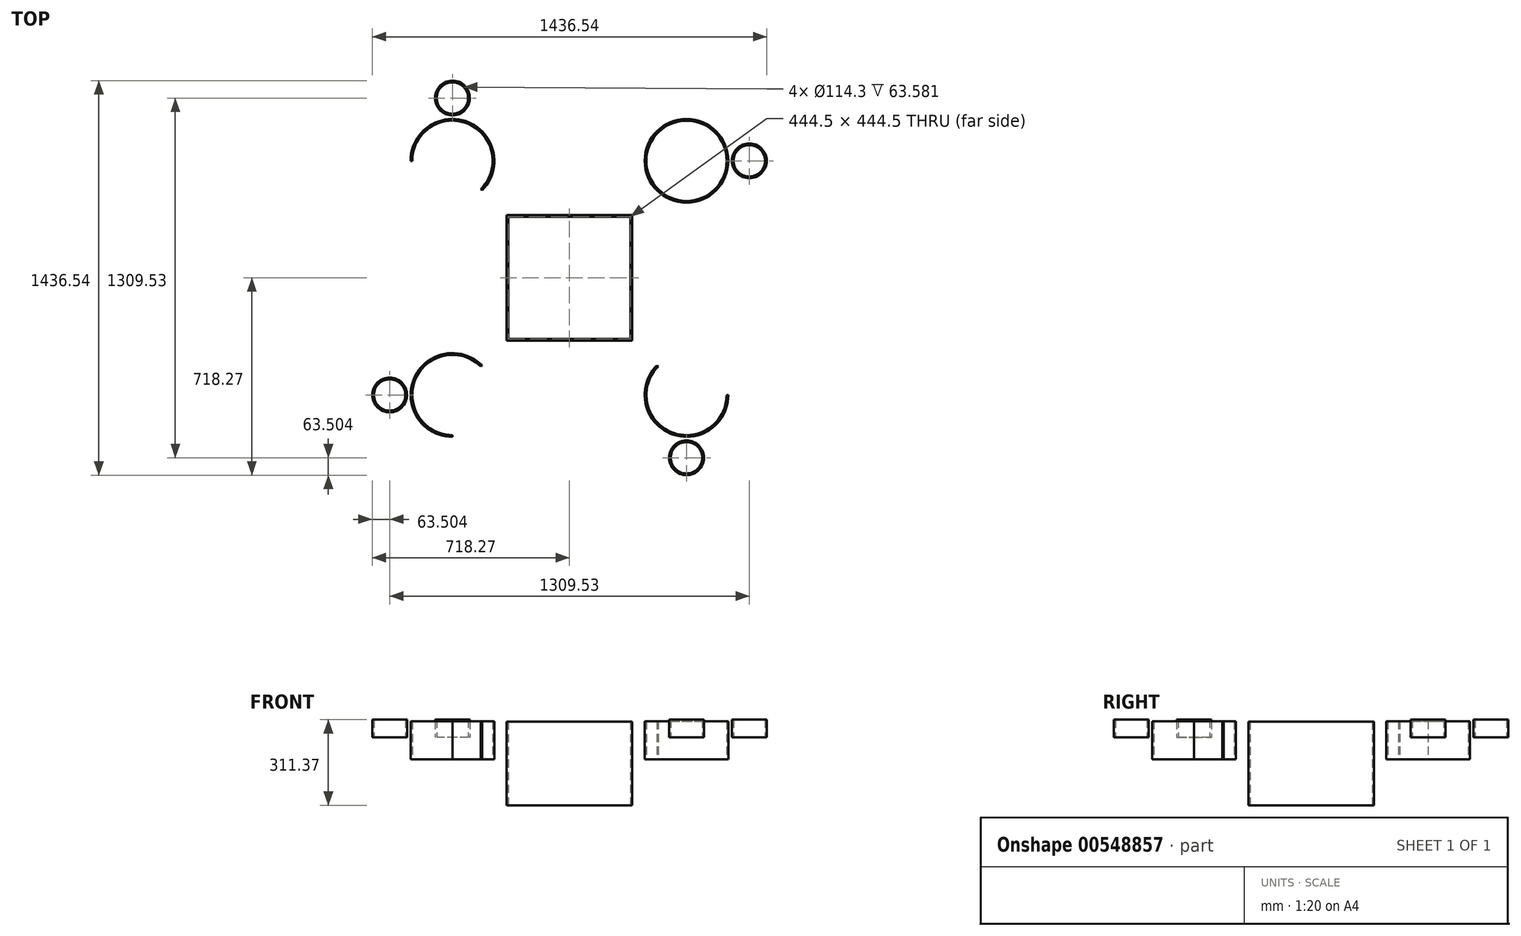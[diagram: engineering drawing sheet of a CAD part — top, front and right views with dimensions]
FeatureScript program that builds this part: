
annotation { "Feature Type Name" : "Feature", "Feature Type Description" : "" }
export const myFeature = defineFeature(function(context is Context, id is Id, definition is map)
    precondition{}
    {
        {
            var Q0;
            Q0=qCreatedBy(makeId("Top.planeOp"),FACE);
            var sketch = newSketch(context, id + "F0", { "sketchPlane" : qUnion([Q0])});
            skLineSegment(sketch, "E0", {"start": v(0, 0) * mm, "end": v(402.27, 0) * mm});
            skLineSegment(sketch, "E1.bottom", {"start": v(228.6, -228.6) * mm, "end": v(-228.6, -228.6) * mm});
            skLineSegment(sketch, "E1.top", {"start": v(228.6, 228.6) * mm, "end": v(-228.6, 228.6) * mm});
            skLineSegment(sketch, "E1.left", {"start": v(228.6, -228.6) * mm, "end": v(228.6, 228.6) * mm});
            skLineSegment(sketch, "E1.right", {"start": v(-228.6, -228.6) * mm, "end": v(-228.6, 228.6) * mm});
            skPoint(sketch, "E1.middle", {"position": v(0, 0) * mm});
            skLineSegment(sketch, "E2", {"start": v(0, 0) * mm, "end": v(228.6, 228.6) * mm});
            skLineSegment(sketch, "E3", {"start": v(228.6, 228.6) * mm, "end": v(426.17, 426.17) * mm});
            skCircle(sketch, "E4", {"center": v(426.17, 426.17) * mm, "radius": 152.4 * mm});
            skLineSegment(sketch, "E5", {"start": v(426.17, 426.17) * mm, "end": v(578.57, 426.17) * mm});
            skLineSegment(sketch, "E6", {"start": v(426.17, 426.17) * mm, "end": v(426.17, 578.57) * mm});
            skLineSegment(sketch, "E7", {"start": v(578.57, 426.17) * mm, "end": v(654.77, 426.17) * mm});
            skCircle(sketch, "E8", {"center": v(654.77, 426.17) * mm, "radius": 63.5 * mm});
            skLineSegment(sketch, "E9.MirrorCS", {"start": v(426.17, 578.57) * mm, "end": v(426.17, 654.77) * mm});
            skCircle(sketch, "E10.MirrorC", {"center": v(426.17, 654.77) * mm, "radius": 63.5 * mm});
            skCircle(sketch, "E11.0", {"center": v(426.17, 426.17) * mm, "radius": 146.05 * mm});
            skCircle(sketch, "E12.0", {"center": v(426.17, 654.77) * mm, "radius": 57.15 * mm});
            skCircle(sketch, "E13.0", {"center": v(654.77, 426.17) * mm, "radius": 57.15 * mm});
            skLineSegment(sketch, "E14.0", {"start": v(222.25, 222.25) * mm, "end": v(-222.25, 222.25) * mm});
            skLineSegment(sketch, "E14.1", {"start": v(222.25, -222.25) * mm, "end": v(222.25, 222.25) * mm});
            skLineSegment(sketch, "E14.2", {"start": v(222.25, -222.25) * mm, "end": v(-222.25, -222.25) * mm});
            skLineSegment(sketch, "E14.3", {"start": v(-222.25, -222.25) * mm, "end": v(-222.25, 222.25) * mm});
            skLineSegment(sketch, "E15.1.0", {"start": v(-426.17, 426.17) * mm, "end": v(-578.57, 426.17) * mm});
            skLineSegment(sketch, "E15.1.1", {"start": v(-426.17, 426.17) * mm, "end": v(-426.17, 578.57) * mm});
            skCircle(sketch, "E15.1.2", {"center": v(-426.17, 654.77) * mm, "radius": 57.15 * mm});
            skLineSegment(sketch, "E15.1.3", {"start": v(-426.17, 426.17) * mm, "end": v(-578.57, 426.17) * mm});
            skCircle(sketch, "E15.1.4", {"center": v(-654.77, 426.17) * mm, "radius": 63.5 * mm});
            skLineSegment(sketch, "E15.1.5", {"start": v(-426.17, 578.57) * mm, "end": v(-426.17, 654.77) * mm});
            skCircle(sketch, "E15.1.6", {"center": v(-426.17, 426.17) * mm, "radius": 146.05 * mm});
            skLineSegment(sketch, "E15.1.7", {"start": v(-228.6, 228.6) * mm, "end": v(-426.17, 426.17) * mm});
            skCircle(sketch, "E15.1.8", {"center": v(-426.17, 654.77) * mm, "radius": 63.5 * mm});
            skLineSegment(sketch, "E15.1.9", {"start": v(-578.57, 426.17) * mm, "end": v(-654.77, 426.17) * mm});
            skCircle(sketch, "E15.1.10", {"center": v(-426.17, 426.17) * mm, "radius": 152.4 * mm});
            skCircle(sketch, "E15.1.11", {"center": v(-654.77, 426.17) * mm, "radius": 57.15 * mm});
            skLineSegment(sketch, "E15.2.0", {"start": v(-426.17, -426.17) * mm, "end": v(-426.17, -578.57) * mm});
            skLineSegment(sketch, "E15.2.1", {"start": v(-426.17, -426.17) * mm, "end": v(-578.57, -426.17) * mm});
            skCircle(sketch, "E15.2.2", {"center": v(-654.77, -426.17) * mm, "radius": 57.15 * mm});
            skLineSegment(sketch, "E15.2.3", {"start": v(-426.17, -426.17) * mm, "end": v(-426.17, -578.57) * mm});
            skCircle(sketch, "E15.2.4", {"center": v(-426.17, -654.77) * mm, "radius": 63.5 * mm});
            skLineSegment(sketch, "E15.2.5", {"start": v(-578.57, -426.17) * mm, "end": v(-654.77, -426.17) * mm});
            skCircle(sketch, "E15.2.6", {"center": v(-426.17, -426.17) * mm, "radius": 146.05 * mm});
            skLineSegment(sketch, "E15.2.7", {"start": v(-228.6, -228.6) * mm, "end": v(-426.17, -426.17) * mm});
            skCircle(sketch, "E15.2.8", {"center": v(-654.77, -426.17) * mm, "radius": 63.5 * mm});
            skLineSegment(sketch, "E15.2.9", {"start": v(-426.17, -578.57) * mm, "end": v(-426.17, -654.77) * mm});
            skCircle(sketch, "E15.2.10", {"center": v(-426.17, -426.17) * mm, "radius": 152.4 * mm});
            skCircle(sketch, "E15.2.11", {"center": v(-426.17, -654.77) * mm, "radius": 57.15 * mm});
            skLineSegment(sketch, "E15.3.0", {"start": v(426.17, -426.17) * mm, "end": v(578.57, -426.17) * mm});
            skLineSegment(sketch, "E15.3.1", {"start": v(426.17, -426.17) * mm, "end": v(426.17, -578.57) * mm});
            skCircle(sketch, "E15.3.2", {"center": v(426.17, -654.77) * mm, "radius": 57.15 * mm});
            skLineSegment(sketch, "E15.3.3", {"start": v(426.17, -426.17) * mm, "end": v(578.57, -426.17) * mm});
            skCircle(sketch, "E15.3.4", {"center": v(654.77, -426.17) * mm, "radius": 63.5 * mm});
            skLineSegment(sketch, "E15.3.5", {"start": v(426.17, -578.57) * mm, "end": v(426.17, -654.77) * mm});
            skCircle(sketch, "E15.3.6", {"center": v(426.17, -426.17) * mm, "radius": 146.05 * mm});
            skLineSegment(sketch, "E15.3.7", {"start": v(228.6, -228.6) * mm, "end": v(426.17, -426.17) * mm});
            skCircle(sketch, "E15.3.8", {"center": v(426.17, -654.77) * mm, "radius": 63.5 * mm});
            skLineSegment(sketch, "E15.3.9", {"start": v(578.57, -426.17) * mm, "end": v(654.77, -426.17) * mm});
            skCircle(sketch, "E15.3.10", {"center": v(426.17, -426.17) * mm, "radius": 152.4 * mm});
            skCircle(sketch, "E15.3.11", {"center": v(654.77, -426.17) * mm, "radius": 57.15 * mm});
            skSolve(sketch);
        }
        {
            var Q0;
            {var subQ1=sQuery(id+"F0.wireOp",EDGE,"E1.bottom");Q0=makeQuery(id+"F0.imprint","IMPRINT",FACE,{"disambiguationData":[TD([[makeQuery(id+"F0.imprint","IMPRINT",EDGE,{"derivedFrom":subQ1}),-1.0]])]});}
            var Q1;
            {var subQ0=sQuery(id+"F0.wireOp",EDGE,"E1.left");var subQ1=sQuery(id+"F0.wireOp",EDGE,"E0");var subQ2=makeQuery(id+"F0.imprint","INTERSECT",VERTEX,{"derivedFrom":[subQ1,subQ0]});Q1=makeQuery(id+"F0.imprint","IMPRINT",FACE,{"disambiguationData":[TD([[makeQuery(id+"F0.imprint","IMPRINT",EDGE,{"disambiguationData":[TD([[subQ2,1.0]])],"derivedFrom":subQ1}),1.0]])]});}
            extrude(context, id + "F1", {"entities" : qUnion([Q0, Q1]), "depth" : 304.8 * mm, "offsetDistance" : 25.4 * mm});
        }
        {
            var Q0;
            {var subQ0=sQuery(id+"F0.wireOp",EDGE,"E15.1.10");var subQ1=sQuery(id+"F0.wireOp",EDGE,"E15.1.1");var subQ2=makeQuery(id+"F0.imprint","INTERSECT",VERTEX,{"derivedFrom":[subQ1,subQ0]});Q0=makeQuery(id+"F0.imprint","IMPRINT",FACE,{"disambiguationData":[TD([[makeQuery(id+"F0.imprint","IMPRINT",EDGE,{"disambiguationData":[TD([[subQ2,1.0]])],"derivedFrom":subQ1}),1.0]])]});}
            var Q1;
            {var subQ0=sQuery(id+"F0.wireOp",EDGE,"E15.1.10");var subQ1=sQuery(id+"F0.wireOp",EDGE,"E15.1.1");var subQ2=makeQuery(id+"F0.imprint","INTERSECT",VERTEX,{"derivedFrom":[subQ1,subQ0]});Q1=makeQuery(id+"F0.imprint","IMPRINT",FACE,{"disambiguationData":[TD([[makeQuery(id+"F0.imprint","IMPRINT",EDGE,{"disambiguationData":[TD([[subQ2,1.0]])],"derivedFrom":subQ1}),-1.0]])]});}
            var Q2;
            {var subQ0=sQuery(id+"F0.wireOp",EDGE,"E15.1.10");var subQ1=sQuery(id+"F0.wireOp",EDGE,"E15.1.3");var subQ2=makeQuery(id+"F0.imprint","INTERSECT",VERTEX,{"derivedFrom":[subQ1,subQ0]});Q2=makeQuery(id+"F0.imprint","IMPRINT",FACE,{"disambiguationData":[TD([[makeQuery(id+"F0.imprint","IMPRINT",EDGE,{"disambiguationData":[TD([[subQ2,1.0]])],"derivedFrom":subQ1}),1.0]])]});}
            var Q3;
            {var subQ0=sQuery(id+"F0.wireOp",EDGE,"E4");var subQ1=sQuery(id+"F0.wireOp",EDGE,"E3");var subQ2=makeQuery(id+"F0.imprint","INTERSECT",VERTEX,{"derivedFrom":[subQ1,subQ0]});Q3=makeQuery(id+"F0.imprint","IMPRINT",FACE,{"disambiguationData":[TD([[makeQuery(id+"F0.imprint","IMPRINT",EDGE,{"disambiguationData":[TD([[subQ2,-1.0]])],"derivedFrom":subQ1}),1.0]])]});}
            var Q4;
            {var subQ0=sQuery(id+"F0.wireOp",EDGE,"E5");var subQ1=sQuery(id+"F0.wireOp",EDGE,"E4");var subQ2=makeQuery(id+"F0.imprint","INTERSECT",VERTEX,{"derivedFrom":[subQ1,subQ0]});Q4=makeQuery(id+"F0.imprint","IMPRINT",FACE,{"disambiguationData":[TD([[makeQuery(id+"F0.imprint","IMPRINT",EDGE,{"disambiguationData":[TD([[subQ2,-1.0]])],"derivedFrom":subQ1}),1.0]])]});}
            var Q5;
            {var subQ0=sQuery(id+"F0.wireOp",EDGE,"E4");var subQ1=sQuery(id+"F0.wireOp",EDGE,"E3");var subQ2=makeQuery(id+"F0.imprint","INTERSECT",VERTEX,{"derivedFrom":[subQ1,subQ0]});Q5=makeQuery(id+"F0.imprint","IMPRINT",FACE,{"disambiguationData":[TD([[makeQuery(id+"F0.imprint","IMPRINT",EDGE,{"disambiguationData":[TD([[subQ2,-1.0]])],"derivedFrom":subQ1}),-1.0]])]});}
            var Q6;
            {var subQ0=sQuery(id+"F0.wireOp",EDGE,"E15.3.10");var subQ1=sQuery(id+"F0.wireOp",EDGE,"E15.3.3");var subQ2=makeQuery(id+"F0.imprint","INTERSECT",VERTEX,{"derivedFrom":[subQ1,subQ0]});Q6=makeQuery(id+"F0.imprint","IMPRINT",FACE,{"disambiguationData":[TD([[makeQuery(id+"F0.imprint","IMPRINT",EDGE,{"disambiguationData":[TD([[subQ2,1.0]])],"derivedFrom":subQ1}),1.0]])]});}
            var Q7;
            {var subQ0=sQuery(id+"F0.wireOp",EDGE,"E15.3.10");var subQ1=sQuery(id+"F0.wireOp",EDGE,"E15.3.1");var subQ2=makeQuery(id+"F0.imprint","INTERSECT",VERTEX,{"derivedFrom":[subQ1,subQ0]});Q7=makeQuery(id+"F0.imprint","IMPRINT",FACE,{"disambiguationData":[TD([[makeQuery(id+"F0.imprint","IMPRINT",EDGE,{"disambiguationData":[TD([[subQ2,1.0]])],"derivedFrom":subQ1}),1.0]])]});}
            var Q8;
            {var subQ0=sQuery(id+"F0.wireOp",EDGE,"E15.3.10");var subQ1=sQuery(id+"F0.wireOp",EDGE,"E15.3.1");var subQ2=makeQuery(id+"F0.imprint","INTERSECT",VERTEX,{"derivedFrom":[subQ1,subQ0]});Q8=makeQuery(id+"F0.imprint","IMPRINT",FACE,{"disambiguationData":[TD([[makeQuery(id+"F0.imprint","IMPRINT",EDGE,{"disambiguationData":[TD([[subQ2,1.0]])],"derivedFrom":subQ1}),-1.0]])]});}
            var Q9;
            {var subQ0=sQuery(id+"F0.wireOp",EDGE,"E15.2.10");var subQ1=sQuery(id+"F0.wireOp",EDGE,"E15.2.1");var subQ2=makeQuery(id+"F0.imprint","INTERSECT",VERTEX,{"derivedFrom":[subQ1,subQ0]});Q9=makeQuery(id+"F0.imprint","IMPRINT",FACE,{"disambiguationData":[TD([[makeQuery(id+"F0.imprint","IMPRINT",EDGE,{"disambiguationData":[TD([[subQ2,1.0]])],"derivedFrom":subQ1}),1.0]])]});}
            var Q10;
            {var subQ0=sQuery(id+"F0.wireOp",EDGE,"E15.2.10");var subQ1=sQuery(id+"F0.wireOp",EDGE,"E15.2.1");var subQ2=makeQuery(id+"F0.imprint","INTERSECT",VERTEX,{"derivedFrom":[subQ1,subQ0]});Q10=makeQuery(id+"F0.imprint","IMPRINT",FACE,{"disambiguationData":[TD([[makeQuery(id+"F0.imprint","IMPRINT",EDGE,{"disambiguationData":[TD([[subQ2,1.0]])],"derivedFrom":subQ1}),-1.0]])]});}
            var Q11;
            {var subQ0=sQuery(id+"F0.wireOp",EDGE,"E15.2.10");var subQ1=sQuery(id+"F0.wireOp",EDGE,"E15.2.3");var subQ2=makeQuery(id+"F0.imprint","INTERSECT",VERTEX,{"derivedFrom":[subQ1,subQ0]});Q11=makeQuery(id+"F0.imprint","IMPRINT",FACE,{"disambiguationData":[TD([[makeQuery(id+"F0.imprint","IMPRINT",EDGE,{"disambiguationData":[TD([[subQ2,1.0]])],"derivedFrom":subQ1}),1.0]])]});}
            extrude(context, id + "F2", {"entities" : qUnion([Q0, Q1, Q2, Q3, Q4, Q5, Q6, Q7, Q8, Q9, Q10, Q11]), "depth" : 305.76 * mm, "offsetDistance" : 25.4 * mm, "hasSecondDirection" : true, "secondDirectionOppositeDirection" : false, "secondDirectionDepth" : 166.62 * mm});
        }
        {
            var Q0;
            Q0=makeQuery(id+"F0.imprint","IMPRINT",FACE,{"disambiguationData":[TD([[makeQuery(id+"F0.imprint","IMPRINT",EDGE,{"derivedFrom":sQuery(id+"F0.wireOp",EDGE,"E15.1.2")}),-1.0]])]});
            var Q1;
            Q1=makeQuery(id+"F0.imprint","IMPRINT",FACE,{"disambiguationData":[TD([[makeQuery(id+"F0.imprint","IMPRINT",EDGE,{"derivedFrom":sQuery(id+"F0.wireOp",EDGE,"E15.1.4")}),-1.0]])]});
            var Q2;
            Q2=makeQuery(id+"F0.imprint","IMPRINT",FACE,{"disambiguationData":[TD([[makeQuery(id+"F0.imprint","IMPRINT",EDGE,{"derivedFrom":sQuery(id+"F0.wireOp",EDGE,"E10.MirrorC")}),-1.0]])]});
            var Q3;
            Q3=makeQuery(id+"F0.imprint","IMPRINT",FACE,{"disambiguationData":[TD([[makeQuery(id+"F0.imprint","IMPRINT",EDGE,{"derivedFrom":sQuery(id+"F0.wireOp",EDGE,"E8")}),1.0]])]});
            var Q4;
            Q4=makeQuery(id+"F0.imprint","IMPRINT",FACE,{"disambiguationData":[TD([[makeQuery(id+"F0.imprint","IMPRINT",EDGE,{"derivedFrom":sQuery(id+"F0.wireOp",EDGE,"E15.3.4")}),-1.0]])]});
            var Q5;
            Q5=makeQuery(id+"F0.imprint","IMPRINT",FACE,{"disambiguationData":[TD([[makeQuery(id+"F0.imprint","IMPRINT",EDGE,{"derivedFrom":sQuery(id+"F0.wireOp",EDGE,"E15.3.2")}),-1.0]])]});
            var Q6;
            Q6=makeQuery(id+"F0.imprint","IMPRINT",FACE,{"disambiguationData":[TD([[makeQuery(id+"F0.imprint","IMPRINT",EDGE,{"derivedFrom":sQuery(id+"F0.wireOp",EDGE,"E15.2.4")}),-1.0]])]});
            var Q7;
            Q7=makeQuery(id+"F0.imprint","IMPRINT",FACE,{"disambiguationData":[TD([[makeQuery(id+"F0.imprint","IMPRINT",EDGE,{"derivedFrom":sQuery(id+"F0.wireOp",EDGE,"E15.2.2")}),-1.0]])]});
            extrude(context, id + "F3", {"entities" : qUnion([Q0, Q1, Q2, Q3, Q4, Q5, Q6, Q7]), "depth" : 311.37 * mm, "offsetDistance" : 25.4 * mm, "hasSecondDirection" : true, "secondDirectionOppositeDirection" : false, "secondDirectionDepth" : 247.79 * mm});
        }
    });
